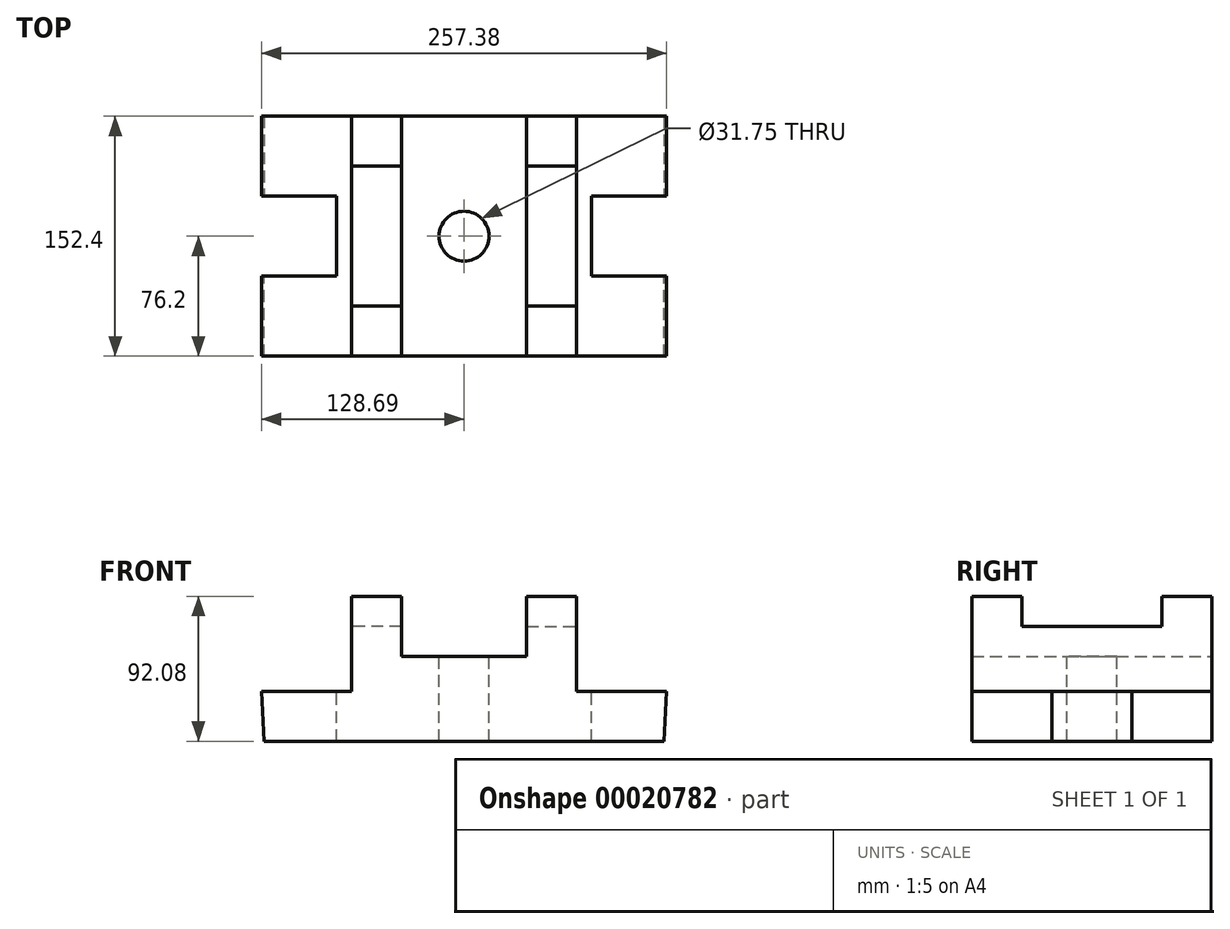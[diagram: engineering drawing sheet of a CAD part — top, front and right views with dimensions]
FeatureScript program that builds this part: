
annotation { "Feature Type Name" : "Feature", "Feature Type Description" : "" }
export const myFeature = defineFeature(function(context is Context, id is Id, definition is map)
    precondition{}
    {
        {
            var Q0;
            Q0=qCreatedBy(makeId("Front.planeOp"),FACE);
            var sketch = newSketch(context, id + "F0", { "sketchPlane" : qUnion([Q0])});
            skLineSegment(sketch, "E0.top", {"start": v(0, -47.39) * mm, "end": v(127, -47.39) * mm});
            skLineSegment(sketch, "E0.right", {"start": v(128.7, -15.64) * mm, "end": v(127, -47.39) * mm});
            skLineSegment(sketch, "E1.bottom", {"start": v(39.8, 44.69) * mm, "end": v(71.54, 44.69) * mm});
            skLineSegment(sketch, "E1.left", {"start": v(39.8, 44.69) * mm, "end": v(39.8, 6.59) * mm});
            skLineSegment(sketch, "E1.right", {"start": v(71.54, 44.69) * mm, "end": v(71.54, -15.64) * mm});
            skLineSegment(sketch, "E2.trimOffspring", {"start": v(71.54, -15.64) * mm, "end": v(128.7, -15.64) * mm});
            skLineSegment(sketch, "E3.bottom", {"start": v(0, 6.59) * mm, "end": v(39.8, 6.59) * mm});
            skLineSegment(sketch, "E4", {"start": v(0, 6.59) * mm, "end": v(0, -47.39) * mm});
            skSolve(sketch);
        }
        {
            var Q0;
            Q0 = qSketchRegion(id + "F0", true);
            extrude(context, id + "F1", {"entities" : qUnion([Q0]), "depth" : 76.2 * mm});
        }
        {
            var Q0;
            Q0=makeQuery(id+"F1.opExtrude","SWEPT_FACE",FACE,{"disambiguationData":[OSD([sQuery(id+"F0.wireOp",EDGE,"E2.trimOffspring")])]});
            var sketch = newSketch(context, id + "F2", { "sketchPlane" : qUnion([Q0])});
            skLineSegment(sketch, "E5.bottom", {"start": v(128.7, 0) * mm, "end": v(71.54, 0) * mm});
            skLineSegment(sketch, "E5.top", {"start": v(128.7, -25.4) * mm, "end": v(71.54, -25.4) * mm});
            skLineSegment(sketch, "E5.left", {"start": v(128.7, 0) * mm, "end": v(128.7, -25.4) * mm});
            skLineSegment(sketch, "E5.right", {"start": v(71.54, 0) * mm, "end": v(71.54, -25.4) * mm});
            skSolve(sketch);
        }
        {
            var Q0;
            Q0=makeQuery(id+"F2.imprint","IMPRINT",FACE,{"disambiguationData":[TD([[makeQuery(id+"F2.imprint","IMPRINT",EDGE,{"derivedFrom":sQuery(id+"F2.wireOp",EDGE,"E5.bottom")}),-1.0]])]});
            extrude(context, id + "F3", {"entities" : qUnion([Q0]), "operationType" : NewBodyOperationType.REMOVE, "oppositeDirection" : true, "depth" : 38.1 * mm});
        }
        {
            var Q0;
            Q0=makeQuery(id+"F1.opExtrude","SWEPT_FACE",FACE,{"disambiguationData":[OSD([sQuery(id+"F0.wireOp",EDGE,"E3.bottom")])]});
            var sketch = newSketch(context, id + "F4", { "sketchPlane" : qUnion([Q0])});
            skArc(sketch, "E6", {"start": v(0, -15.87) * mm, "mid": v(11.23, -11.23) * mm, "end": v(15.87, 0) * mm});
            skLineSegment(sketch, "E7", {"start": v(15.87, 0) * mm, "end": v(0, 0) * mm});
            skLineSegment(sketch, "E8", {"start": v(0, -15.87) * mm, "end": v(0, 0) * mm});
            skSolve(sketch);
        }
        {
            var Q0;
            {var subQ0=sQuery(id+"F0.wireOp",EDGE,"E3.bottom");var subQ1=makeQuery(id+"F1.opExtrude","CAP_EDGE",EDGE,{"disambiguationData":[OSD([subQ0])],"isStart":true});var subQ2=sQuery(id+"F4.wireOp",EDGE,"E6");var subQ3=makeQuery(id+"F4.imprint","INTERSECT",VERTEX,{"derivedFrom":[subQ1,subQ2]});Q0=makeQuery(id+"F4.imprint","IMPRINT",FACE,{"disambiguationData":[TD([[makeQuery(id+"F4.imprint","IMPRINT",EDGE,{"disambiguationData":[TD([[subQ3,-1.0]])],"derivedFrom":subQ2}),1.0]])]});}
            extrude(context, id + "F5", {"entities" : qUnion([Q0]), "operationType" : NewBodyOperationType.REMOVE, "oppositeDirection" : true, "depth" : 53.97 * mm});
        }
        {
            var Q0;
            Q0=makeQuery(id+"F1.opExtrude","SWEPT_BODY",BODY,{"disambiguationData":[OSD([sQuery(id+"F0.wireOp",EDGE,"E0.top"),sQuery(id+"F0.wireOp",EDGE,"E0.right"),sQuery(id+"F0.wireOp",EDGE,"E1.bottom"),sQuery(id+"F0.wireOp",EDGE,"E1.left"),sQuery(id+"F0.wireOp",EDGE,"E1.right"),sQuery(id+"F0.wireOp",EDGE,"E2.trimOffspring"),sQuery(id+"F0.wireOp",EDGE,"E3.bottom"),sQuery(id+"F0.wireOp",EDGE,"E4")])]});
            var Q1;
            Q1=makeQuery(id+"F1.opExtrude","SWEPT_FACE",FACE,{"disambiguationData":[OSD([sQuery(id+"F0.wireOp",EDGE,"E4")])]});
            mirror(context, id + "F6", {"operationType" : NewBodyOperationType.ADD, "entities" : qUnion([Q0]), "mirrorPlane" : qUnion([Q1])});
        }
        {
            var Q0;
            Q0=makeQuery(id+"F1.opExtrude","SWEPT_BODY",BODY,{"disambiguationData":[OSD([sQuery(id+"F0.wireOp",EDGE,"E0.top"),sQuery(id+"F0.wireOp",EDGE,"E0.right"),sQuery(id+"F0.wireOp",EDGE,"E1.bottom"),sQuery(id+"F0.wireOp",EDGE,"E1.left"),sQuery(id+"F0.wireOp",EDGE,"E1.right"),sQuery(id+"F0.wireOp",EDGE,"E2.trimOffspring"),sQuery(id+"F0.wireOp",EDGE,"E3.bottom"),sQuery(id+"F0.wireOp",EDGE,"E4")])]});
            var Q1;
            Q1=makeQuery(id+"F0.imprint","IMPRINT",FACE,{"disambiguationData":[TD([[makeQuery(id+"F0.imprint","IMPRINT",EDGE,{"derivedFrom":sQuery(id+"F0.wireOp",EDGE,"E0.top")}),1.0]])]});
            mirror(context, id + "F7", {"operationType" : NewBodyOperationType.ADD, "entities" : qUnion([Q0]), "mirrorPlane" : qUnion([Q1])});
        }
        {
            var Q0;
            {var subQ0=makeQuery(id+"F6.opPattern","COPY",FACE,{"derivedFrom":makeQuery(id+"F3.boolean.opBoolean","MERGE",FACE,{"derivedFrom":[makeQuery(id+"F1.opExtrude","SWEPT_FACE",FACE,{"disambiguationData":[OSD([sQuery(id+"F0.wireOp",EDGE,"E1.right")])]}),makeQuery(id+"F3.opExtrude","SWEPT_FACE",FACE,{"disambiguationData":[OSD([sQuery(id+"F2.wireOp",EDGE,"E5.right")])]})]}),"instanceName":"1"});Q0=makeQuery(id+"F7.boolean.opBoolean","MERGE",FACE,{"derivedFrom":[subQ0,makeQuery(id+"F7.opPattern","COPY",FACE,{"derivedFrom":subQ0,"instanceName":"1"})]});}
            var sketch = newSketch(context, id + "F8", { "sketchPlane" : qUnion([Q0])});
            skLineSegment(sketch, "E9.bottom", {"start": v(-25.4, -15.64) * mm, "end": v(25.4, -15.64) * mm});
            skLineSegment(sketch, "E9.top", {"start": v(-25.4, -47.39) * mm, "end": v(25.4, -47.39) * mm});
            skLineSegment(sketch, "E9.left", {"start": v(-25.4, -15.64) * mm, "end": v(-25.4, -47.39) * mm});
            skLineSegment(sketch, "E9.right", {"start": v(25.4, -15.64) * mm, "end": v(25.4, -47.39) * mm});
            skSolve(sketch);
        }
        {
            var Q0;
            Q0 = qSketchRegion(id + "F8", true);
            var Q1;
            Q1=makeQuery(id+"F8.imprint","IMPRINT",FACE,{"disambiguationData":[TD([[makeQuery(id+"F8.imprint","IMPRINT",EDGE,{"derivedFrom":sQuery(id+"F8.wireOp",EDGE,"E9.bottom")}),-1.0]])]});
            extrude(context, id + "F9", {"entities" : qUnion([Q0, Q1]), "operationType" : NewBodyOperationType.ADD, "depth" : 9.52 * mm});
        }
        {
            var Q0;
            {var subQ0=makeQuery(id+"F3.boolean.opBoolean","MERGE",FACE,{"derivedFrom":[makeQuery(id+"F1.opExtrude","SWEPT_FACE",FACE,{"disambiguationData":[OSD([sQuery(id+"F0.wireOp",EDGE,"E1.right")])]}),makeQuery(id+"F3.opExtrude","SWEPT_FACE",FACE,{"disambiguationData":[OSD([sQuery(id+"F2.wireOp",EDGE,"E5.right")])]})]});Q0=makeQuery(id+"F7.boolean.opBoolean","MERGE",FACE,{"derivedFrom":[subQ0,makeQuery(id+"F7.opPattern","COPY",FACE,{"derivedFrom":subQ0,"instanceName":"1"})]});}
            var sketch = newSketch(context, id + "F10", { "sketchPlane" : qUnion([Q0])});
            skLineSegment(sketch, "E10.bottom", {"start": v(-25.4, -15.64) * mm, "end": v(25.4, -15.64) * mm});
            skLineSegment(sketch, "E10.top", {"start": v(-25.4, -47.39) * mm, "end": v(25.4, -47.39) * mm});
            skLineSegment(sketch, "E10.left", {"start": v(-25.4, -15.64) * mm, "end": v(-25.4, -47.39) * mm});
            skLineSegment(sketch, "E10.right", {"start": v(25.4, -15.64) * mm, "end": v(25.4, -47.39) * mm});
            skSolve(sketch);
        }
        {
            var Q0;
            Q0=makeQuery(id+"F10.imprint","IMPRINT",FACE,{"disambiguationData":[TD([[makeQuery(id+"F10.imprint","IMPRINT",EDGE,{"derivedFrom":sQuery(id+"F10.wireOp",EDGE,"E10.bottom")}),-1.0]])]});
            extrude(context, id + "F11", {"entities" : qUnion([Q0]), "operationType" : NewBodyOperationType.ADD, "depth" : 9.52 * mm});
        }
        {
            var Q0;
            {var subQ0=makeQuery(id+"F6.opPattern","COPY",FACE,{"derivedFrom":makeQuery(id+"F1.opExtrude","SWEPT_FACE",FACE,{"disambiguationData":[OSD([sQuery(id+"F0.wireOp",EDGE,"E1.bottom")])]}),"instanceName":"1"});Q0=makeQuery(id+"F7.boolean.opBoolean","MERGE",FACE,{"derivedFrom":[subQ0,makeQuery(id+"F7.opPattern","COPY",FACE,{"derivedFrom":subQ0,"instanceName":"1"})]});}
            var sketch = newSketch(context, id + "F12", { "sketchPlane" : qUnion([Q0])});
            skLineSegment(sketch, "E11.bottom", {"start": v(-39.8, 44.45) * mm, "end": v(-71.54, 44.45) * mm});
            skLineSegment(sketch, "E11.top", {"start": v(-39.8, -44.45) * mm, "end": v(-71.54, -44.45) * mm});
            skLineSegment(sketch, "E11.left", {"start": v(-39.8, 44.45) * mm, "end": v(-39.8, -44.45) * mm});
            skLineSegment(sketch, "E11.right", {"start": v(-71.54, 44.45) * mm, "end": v(-71.54, -44.45) * mm});
            skLineSegment(sketch, "E12", {"start": v(-39.8, 44.45) * mm, "end": v(-39.8, 76.2) * mm});
            skSolve(sketch);
        }
        {
            var Q0;
            Q0 = qSketchRegion(id + "F12", true);
            extrude(context, id + "F13", {"entities" : qUnion([Q0]), "operationType" : NewBodyOperationType.REMOVE, "oppositeDirection" : true, "depth" : 19.05 * mm});
        }
        {
            var Q0;
            {var subQ0=makeQuery(id+"F1.opExtrude","SWEPT_FACE",FACE,{"disambiguationData":[OSD([sQuery(id+"F0.wireOp",EDGE,"E1.bottom")])]});Q0=makeQuery(id+"F7.boolean.opBoolean","MERGE",FACE,{"derivedFrom":[subQ0,makeQuery(id+"F7.opPattern","COPY",FACE,{"derivedFrom":subQ0,"instanceName":"1"})]});}
            var sketch = newSketch(context, id + "F14", { "sketchPlane" : qUnion([Q0])});
            skLineSegment(sketch, "E13.bottom", {"start": v(39.8, 44.45) * mm, "end": v(71.54, 44.45) * mm});
            skLineSegment(sketch, "E13.top", {"start": v(39.8, -44.45) * mm, "end": v(71.54, -44.45) * mm});
            skLineSegment(sketch, "E13.left", {"start": v(39.8, 44.45) * mm, "end": v(39.8, -44.45) * mm});
            skLineSegment(sketch, "E13.right", {"start": v(71.54, 44.45) * mm, "end": v(71.54, -44.45) * mm});
            skLineSegment(sketch, "E14", {"start": v(71.54, 44.45) * mm, "end": v(71.54, 76.2) * mm});
            skSolve(sketch);
        }
        {
            var Q0;
            Q0 = qSketchRegion(id + "F14", true);
            extrude(context, id + "F15", {"entities" : qUnion([Q0]), "operationType" : NewBodyOperationType.REMOVE, "oppositeDirection" : true, "depth" : 19.05 * mm});
        }
    });
